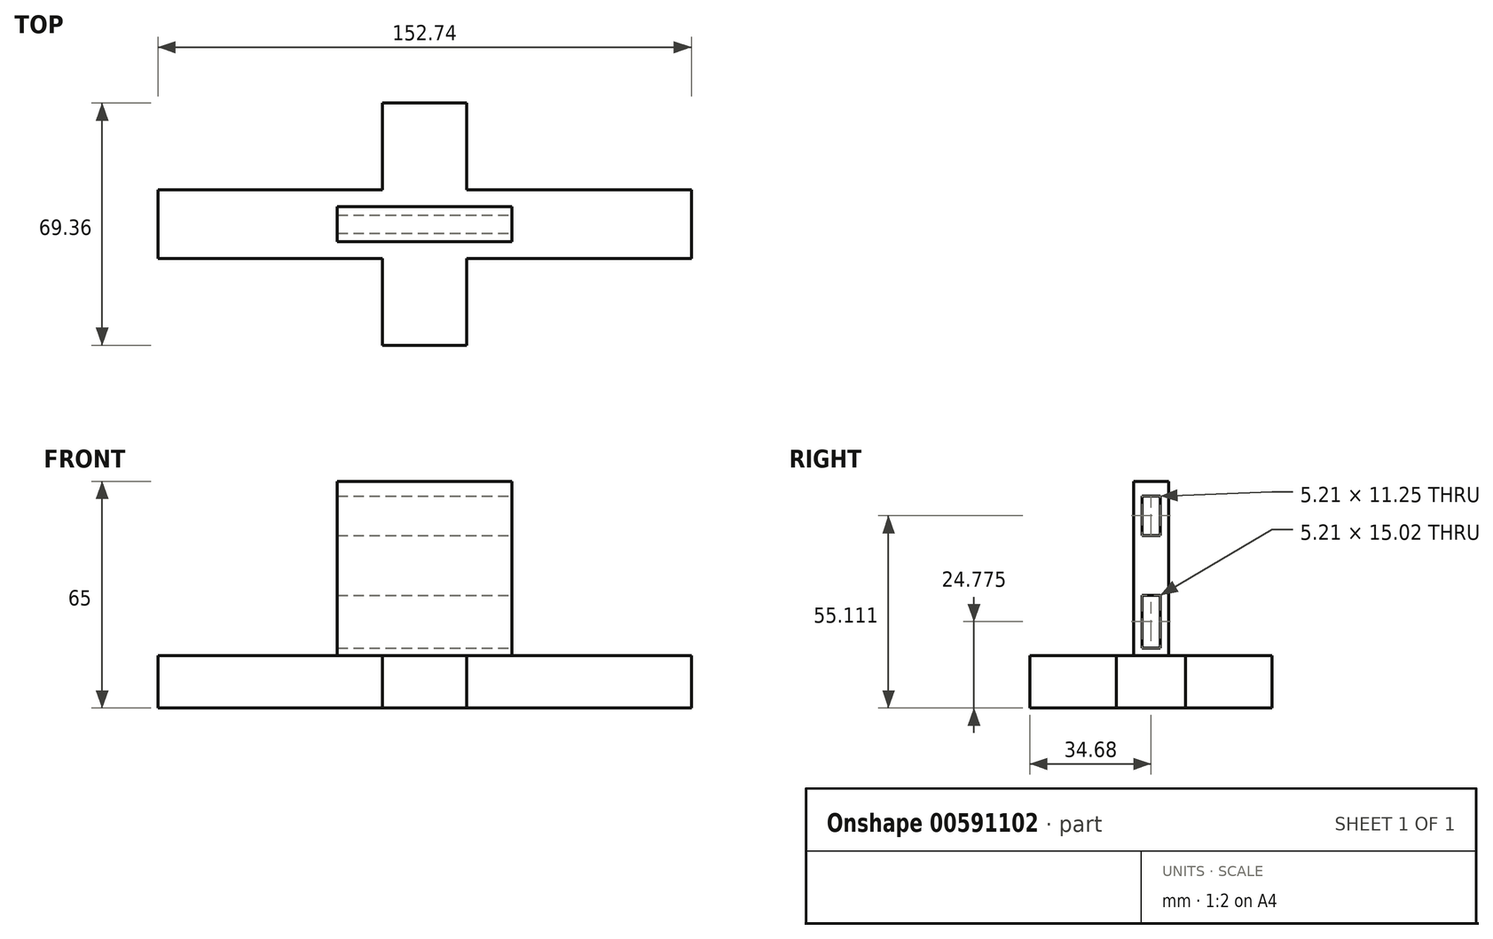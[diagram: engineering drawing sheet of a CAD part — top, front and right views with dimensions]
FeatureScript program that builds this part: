
annotation { "Feature Type Name" : "Feature", "Feature Type Description" : "" }
export const myFeature = defineFeature(function(context is Context, id is Id, definition is map)
    precondition{}
    {
        {
            var Q0;
            Q0=qCreatedBy(makeId("Top.planeOp"),FACE);
            var sketch = newSketch(context, id + "F0", { "sketchPlane" : qUnion([Q0])});
            skLineSegment(sketch, "E0.bottom", {"start": v(76.37, 9.86) * mm, "end": v(-76.37, 9.86) * mm});
            skLineSegment(sketch, "E0.top", {"start": v(76.37, -9.86) * mm, "end": v(-76.37, -9.86) * mm});
            skLineSegment(sketch, "E0.left", {"start": v(76.37, 9.86) * mm, "end": v(76.37, -9.86) * mm});
            skLineSegment(sketch, "E0.right", {"start": v(-76.37, 9.86) * mm, "end": v(-76.37, -9.86) * mm});
            skPoint(sketch, "E0.middle", {"position": v(0, 0) * mm});
            skLineSegment(sketch, "E1.bottom", {"start": v(12.1, 34.68) * mm, "end": v(-12.1, 34.68) * mm});
            skLineSegment(sketch, "E1.top", {"start": v(12.1, -34.68) * mm, "end": v(-12.1, -34.68) * mm});
            skLineSegment(sketch, "E1.left", {"start": v(12.1, 34.68) * mm, "end": v(12.1, -34.68) * mm});
            skLineSegment(sketch, "E1.right", {"start": v(-12.1, 34.68) * mm, "end": v(-12.1, -34.68) * mm});
            skSolve(sketch);
        }
        {
            var Q0;
            Q0 = qSketchRegion(id + "F0", true);
            extrude(context, id + "F1", {"entities" : qUnion([Q0]), "depth" : 15 * mm, "offsetDistance" : 25 * mm});
        }
        {
            var Q0;
            Q0=makeQuery(id+"F1.opExtrude","CAP_FACE",FACE,{"disambiguationData":[OSD([sQuery(id+"F0.wireOp",EDGE,"E0.bottom"),sQuery(id+"F0.wireOp",EDGE,"E0.top"),sQuery(id+"F0.wireOp",EDGE,"E0.left"),sQuery(id+"F0.wireOp",EDGE,"E0.right"),sQuery(id+"F0.wireOp",EDGE,"E1.bottom"),sQuery(id+"F0.wireOp",EDGE,"E1.top"),sQuery(id+"F0.wireOp",EDGE,"E1.left"),sQuery(id+"F0.wireOp",EDGE,"E1.right")])],"isStart":false});
            var sketch = newSketch(context, id + "F2", { "sketchPlane" : qUnion([Q0])});
            skLineSegment(sketch, "E2.bottom", {"start": v(25, 5) * mm, "end": v(-25, 5) * mm});
            skLineSegment(sketch, "E2.top", {"start": v(25, -5) * mm, "end": v(-25, -5) * mm});
            skLineSegment(sketch, "E2.left", {"start": v(25, 5) * mm, "end": v(25, -5) * mm});
            skLineSegment(sketch, "E2.right", {"start": v(-25, 5) * mm, "end": v(-25, -5) * mm});
            skPoint(sketch, "E2.middle", {"position": v(0, 0) * mm});
            skSolve(sketch);
        }
        {
            var Q0;
            Q0 = qSketchRegion(id + "F2", true);
            extrude(context, id + "F3", {"entities" : qUnion([Q0]), "operationType" : NewBodyOperationType.ADD, "depth" : 50 * mm, "offsetDistance" : 25 * mm});
        }
        {
            var Q0;
            Q0=makeQuery(id+"F3.opExtrude","SWEPT_FACE",FACE,{"disambiguationData":[OSD([sQuery(id+"F2.wireOp",EDGE,"E2.left")])]});
            var sketch = newSketch(context, id + "F4", { "sketchPlane" : qUnion([Q0])});
            skLineSegment(sketch, "E3", {"start": v(5, 40) * mm, "end": v(-5, 40) * mm});
            skLineSegment(sketch, "E4", {"start": v(-5, 40) * mm, "end": v(0, 40) * mm});
            skLineSegment(sketch, "E5", {"start": v(0, 40) * mm, "end": v(0, 15) * mm});
            skLineSegment(sketch, "E6", {"start": v(0, 15) * mm, "end": v(0, 40) * mm});
            skLineSegment(sketch, "E7", {"start": v(0, 40) * mm, "end": v(0, 65) * mm});
            skLineSegment(sketch, "E8.bottom", {"start": v(2.6, 49.48) * mm, "end": v(-2.6, 49.48) * mm});
            skLineSegment(sketch, "E8.top", {"start": v(2.6, 60.74) * mm, "end": v(-2.6, 60.74) * mm});
            skLineSegment(sketch, "E8.left", {"start": v(2.6, 49.48) * mm, "end": v(2.6, 60.74) * mm});
            skLineSegment(sketch, "E8.right", {"start": v(-2.6, 49.48) * mm, "end": v(-2.6, 60.74) * mm});
            skPoint(sketch, "E8.middle", {"position": v(0, 55.11) * mm});
            skLineSegment(sketch, "E9.bottom", {"start": v(2.6, 32.29) * mm, "end": v(-2.6, 32.29) * mm});
            skLineSegment(sketch, "E9.top", {"start": v(2.6, 17.26) * mm, "end": v(-2.6, 17.26) * mm});
            skLineSegment(sketch, "E9.left", {"start": v(2.6, 32.29) * mm, "end": v(2.6, 17.26) * mm});
            skLineSegment(sketch, "E9.right", {"start": v(-2.6, 32.29) * mm, "end": v(-2.6, 17.26) * mm});
            skSolve(sketch);
        }
        {
            var Q0;
            Q0 = qSketchRegion(id + "F4", true);
            extrude(context, id + "F5", {"entities" : qUnion([Q0]), "operationType" : NewBodyOperationType.REMOVE, "oppositeDirection" : true, "depth" : 100 * mm, "offsetDistance" : 25 * mm});
        }
    });
